# Revit family: LWplc_Latchwaysplc_WrkngPltfrmAndWlkwySym_WalkSafe_PermanentlyFixedRoofLadderSystem
name_source: partatom
category: Specialty Equipment
revit_build: Autodesk Revit 2013 (Build: 20121003_2115(x64)
units: mm (PartAtom-declared; Revit-internal decimal feet)

## types (5) — shared parameters
AssetType = Movable
Default Elevation = 1219 mm
Description = Latchways ManSafe® for Roofing, using WalkSafe
DurationUnit = year
FireExit = No
IfcExportAs = NOTDEFINED
IfcExportType = IfcTransportElement
Length = 3000 mm  [stored 9.84252 ft]
ManufacturerName = Latchways plc
ManufacturerURL = www.latchways.com
Material = PVC-U
NBSDescription = Working platform and walkway system
NBSReference = 30-05-30/195
NominalLength = 3000 mm  [stored 9.84252 ft]
TreadDepth = 24 mm  [stored 0.0787402 ft]
URL = www.latchways.com
Uniclass2 = Ss_35_10_30_95
Version = 1
WarrantyDurationUnit = year

## per-type parameters (varying)
| type | BIMObjectName | BaseDepth | BaseMaterial | Model | ModelNumber | ModelReference | Name | NominalHeight | NominalWidth | ProductInformation | Size | TreadPattern | Width |
| WorkingPlatformAndWalkwaySystem_WalkSafe_InlineCrown_Latchwaysplc | LWplc_Latchwaysplc_WorkingPlatformAndWalkWaySystem_WalkSafe_BUOSInlineCrown | 58 mm  [stored 0.190289 ft] | <By Category> | 66002-00 | 66002-00 | Walksafe - BUOS-Comp Roof - Inline with Crown | WorkingPlatformAndWalkingSystem_WalkSafe_InlineCrown_Latchwaysplc | 83 mm  [stored 0.27231 ft] | 630 mm  [stored 2.06693 ft] | www.latchways.com/BIM/66002-00_Walksafe_BUOS_Comp_InLineWithCrown.pdf | 630 x 3000 x 83 mm | LWplc_Latchwaysplc_PVC_InlineTread | 630 mm  [stored 2.06693 ft] |
| WorkingPlatformAndWalkwaySystem_WalkSafe_AcrossCrown_Latchwaysplc | LWplc_Latchwaysplc_WorkingPlatformAndWalkwaySystem_WalkSafe_BUOSAcrossCrown | 58 mm  [stored 0.190289 ft] | LWplc_Latchways_PVC | 66001-00 | 66001-00 | Walksafe - BUOS-Comp Roof - Across Crown | WorkingPlatformAndWalkingSystem_WalkSafe_AcrossCrown_Latchwaysplc | 83 mm  [stored 0.27231 ft] | 630 mm  [stored 2.06693 ft] | www.latchways.com/BIM/66001-00_Walksafe_BUOS_Comp_AcrossCrown.pdf | 630 x 3000 x 83 mm | LWplc_Latchwaysplc_PVC_AcrossTread | 630 mm  [stored 2.06693 ft] |
| WorkingPlatformAndWalkwaySystem_WalkSafe_FlatRoof_Latchwaysplc | LWplc_Latchwaysplc_WorkingPlatformAndWalkwaySystem_WalkSafe_FlatRoof | 50 mm  [stored 0.164042 ft] | <By Category> | 66006-00 | 66006-00 | Walksafe - Single Ply Flat Roof | WorkingPlatformAndWalkingSystem_WalkSafe_FlatRoof_Latchwaysplc | 50 mm  [stored 0.164042 ft] | 600 mm | www.latchways.com/BIM/66006-00_Walksafe_SinglePlyMembrane.pdf | 600 x 3000 x 50 mm | LWplc_Latchwaysplc_PVC_InlineTread | 600 mm |
| WorkingPlatformAndWalkwaySystem_WalkSafe_AcrossSeam_Latchwaysplc | LWplc_Latchwaysplc_WorkingPlatformAndWalkwaySystem_WalkSafeAcrossSeam | 58 mm  [stored 0.190289 ft] | <By Category> | 66001-00 | 66001-00 | Walksafe - Standing Seam Roof - Across Seam | WorkingPlatformAndWalkingSystem_WalkSafe_AcrossSeam_Latchwaysplc | 83 mm  [stored 0.27231 ft] | 630 mm  [stored 2.06693 ft] | www.latchways.com/BIM/66001-00_Walksafe_StandingSeam_AcrossSeams.pdf | 630 x 3000 x 83 mm | LWplc_Latchwaysplc_PVC_AcrossTread | 630 mm  [stored 2.06693 ft] |
| WorkingPlatformAndWalkwaySystem_WalkSafe_InlineSeam_Latchwaysplc | LWplc_Latchwaysplc_WorkingPlatformAndWalkwaySystem_WalkSafe_InlineSeam | 58 mm  [stored 0.190289 ft] | <By Category> | 66002-00 | 66002-00 | Walksafe - Standing Seam Roof - Inline with Seam | WorkingPlatformAndWalkingSystem_WalkSafe_InlineSeam_Latchwaysplc | 83 mm  [stored 0.27231 ft] | 630 mm  [stored 2.06693 ft] | www.latchways.com/BIM/66002-00_Walksafe_StandingSeam_InLineWithSeams.pdf | 630 x 3000 x 83 mm | LWplc_Latchwaysplc_PVC_InlineTread | 630 mm  [stored 2.06693 ft] |

note: [stored X ft] marks values corroborated as IEEE doubles in the binary element streams (Revit-internal decimal feet)

## geometry (parser evidence)
native form markers: Blend x9, Sweep x1
no freeform markers — native parametric forms only
